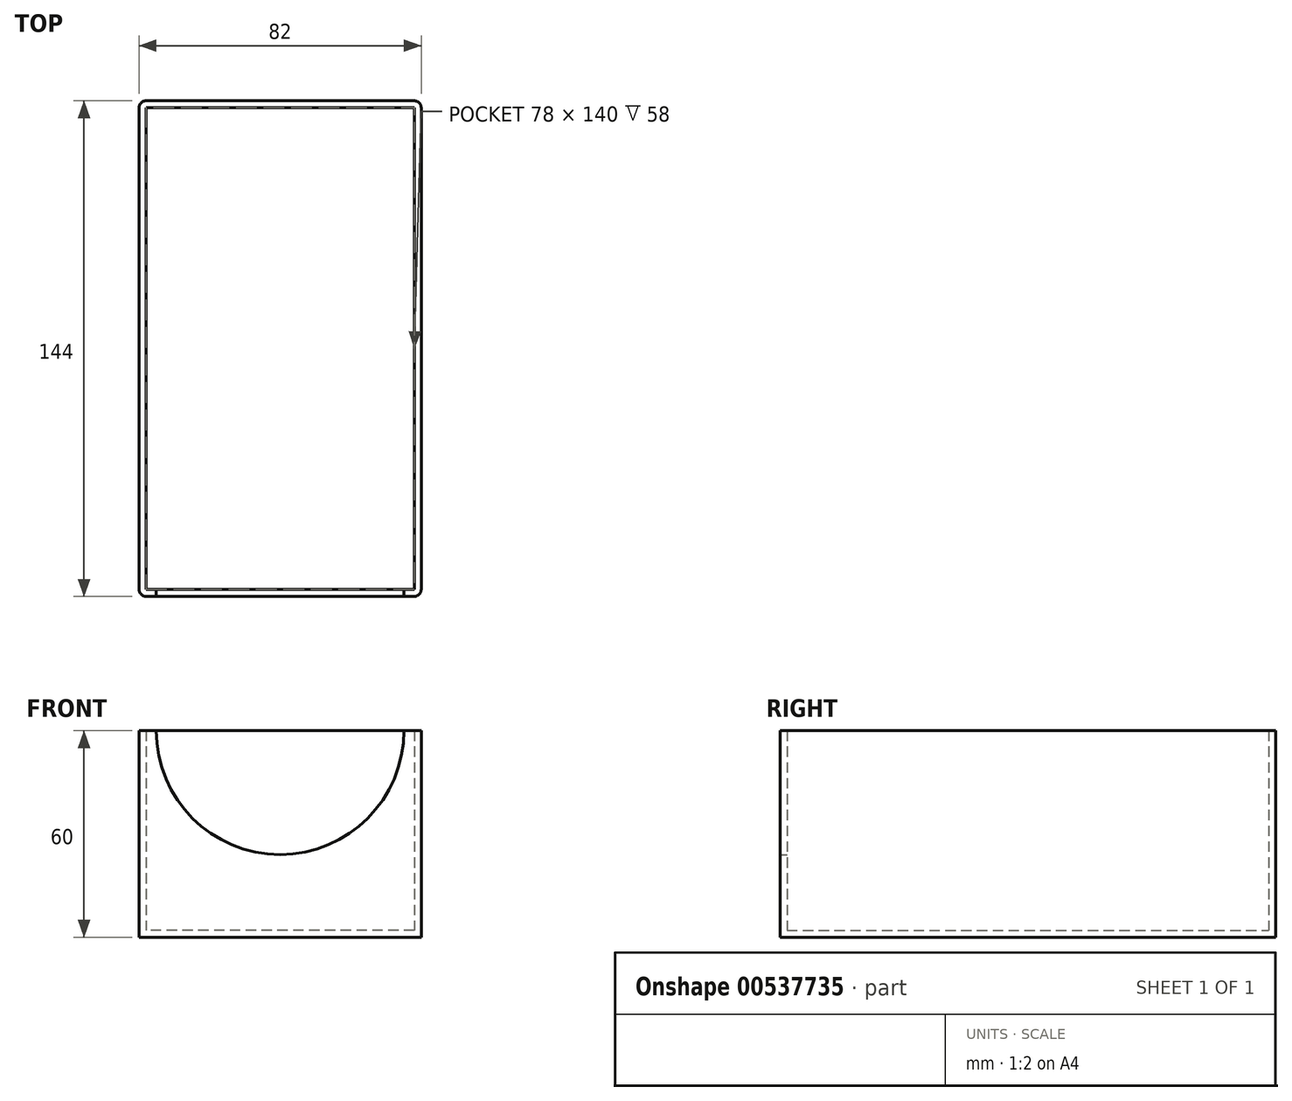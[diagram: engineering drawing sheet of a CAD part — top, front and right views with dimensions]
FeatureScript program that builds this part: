
annotation { "Feature Type Name" : "Feature", "Feature Type Description" : "" }
export const myFeature = defineFeature(function(context is Context, id is Id, definition is map)
    precondition{}
    {
        {
            var Q0;
            Q0=qCreatedBy(makeId("Top.planeOp"),FACE);
            var sketch = newSketch(context, id + "F0", { "sketchPlane" : qUnion([Q0])});
            skLineSegment(sketch, "E0.bottom", {"start": v(39, -70) * mm, "end": v(-39, -70) * mm});
            skLineSegment(sketch, "E0.top", {"start": v(39, 70) * mm, "end": v(-39, 70) * mm});
            skLineSegment(sketch, "E0.left", {"start": v(39, -70) * mm, "end": v(39, 70) * mm});
            skLineSegment(sketch, "E0.right", {"start": v(-39, -70) * mm, "end": v(-39, 70) * mm});
            skPoint(sketch, "E0.middle", {"position": v(0, 0) * mm});
            skLineSegment(sketch, "E1.0", {"start": v(-41, -72) * mm, "end": v(-41, 72) * mm});
            skLineSegment(sketch, "E1.1", {"start": v(41, -72) * mm, "end": v(-41, -72) * mm});
            skLineSegment(sketch, "E1.2", {"start": v(41, -72) * mm, "end": v(41, 72) * mm});
            skLineSegment(sketch, "E1.3", {"start": v(41, 72) * mm, "end": v(-41, 72) * mm});
            skSolve(sketch);
        }
        {
            var Q0;
            Q0=makeQuery(id+"F0.imprint","IMPRINT",FACE,{"disambiguationData":[TD([[makeQuery(id+"F0.imprint","IMPRINT",EDGE,{"derivedFrom":sQuery(id+"F0.wireOp",EDGE,"59183aea-21e8-4340-b351-88ff4695227d.0")}),-1.0]])]});
            var Q1;
            Q1=makeQuery(id+"F0.imprint","IMPRINT",FACE,{"disambiguationData":[TD([[makeQuery(id+"F0.imprint","IMPRINT",EDGE,{"derivedFrom":sQuery(id+"F0.wireOp",EDGE,"E0.bottom")}),-1.0]])]});
            extrude(context, id + "F1", {"entities" : qUnion([Q0, Q1]), "depth" : 2 * mm, "offsetDistance" : 25 * mm});
        }
        {
            var Q0;
            Q0=makeQuery(id+"F0.imprint","IMPRINT",FACE,{"disambiguationData":[TD([[makeQuery(id+"F0.imprint","IMPRINT",EDGE,{"derivedFrom":sQuery(id+"F0.wireOp",EDGE,"E0.bottom")}),1.0]])]});
            extrude(context, id + "F2", {"entities" : qUnion([Q0]), "operationType" : NewBodyOperationType.ADD, "depth" : 60 * mm, "offsetDistance" : 25 * mm});
        }
        {
            var Q0;
            Q0=makeQuery(id+"F2.opExtrude","SWEPT_FACE",FACE,{"disambiguationData":[OSD([sQuery(id+"F0.wireOp",EDGE,"E0.bottom")])]});
            var sketch = newSketch(context, id + "F3", { "sketchPlane" : qUnion([Q0])});
            skArc(sketch, "E2", {"start": v(-36, 60) * mm, "mid": v(0, 24) * mm, "end": v(36, 60) * mm});
            skSolve(sketch);
        }
        {
            var Q0;
            {var subQ0=sQuery(id+"F3.wireOp",EDGE,"E2");Q0=makeQuery(id+"F3.imprint","IMPRINT",FACE,{"disambiguationData":[TD([[makeQuery(id+"F3.imprint","IMPRINT",EDGE,{"derivedFrom":subQ0}),1.0]])]});}
            extrude(context, id + "F4", {"entities" : qUnion([Q0]), "operationType" : NewBodyOperationType.REMOVE, "oppositeDirection" : true, "depth" : 25 * mm, "offsetDistance" : 25 * mm});
        }
        {
            var Q0;
            Q0=makeQuery(id+"F2.opExtrude","SWEPT_EDGE",EDGE,{"disambiguationData":[OSD([sQuery(id+"F0.wireOp",EDGE,"E1.0"),sQuery(id+"F0.wireOp",EDGE,"E1.3")])]});
            var Q1;
            Q1=makeQuery(id+"F2.opExtrude","SWEPT_EDGE",EDGE,{"disambiguationData":[OSD([sQuery(id+"F0.wireOp",EDGE,"E1.2"),sQuery(id+"F0.wireOp",EDGE,"E1.3")])]});
            var Q2;
            Q2=makeQuery(id+"F2.opExtrude","SWEPT_EDGE",EDGE,{"disambiguationData":[OSD([sQuery(id+"F0.wireOp",EDGE,"E1.0"),sQuery(id+"F0.wireOp",EDGE,"E1.1")])]});
            var Q3;
            Q3=makeQuery(id+"F2.opExtrude","SWEPT_EDGE",EDGE,{"disambiguationData":[OSD([sQuery(id+"F0.wireOp",EDGE,"E1.1"),sQuery(id+"F0.wireOp",EDGE,"E1.2")])]});
            fillet(context, id + "F5", {"entities" : qUnion([Q0, Q1, Q2, Q3]), "radius" : 2 * mm, "tangentPropagation" : true, "allowEdgeOverflow" : false});
        }
    });
